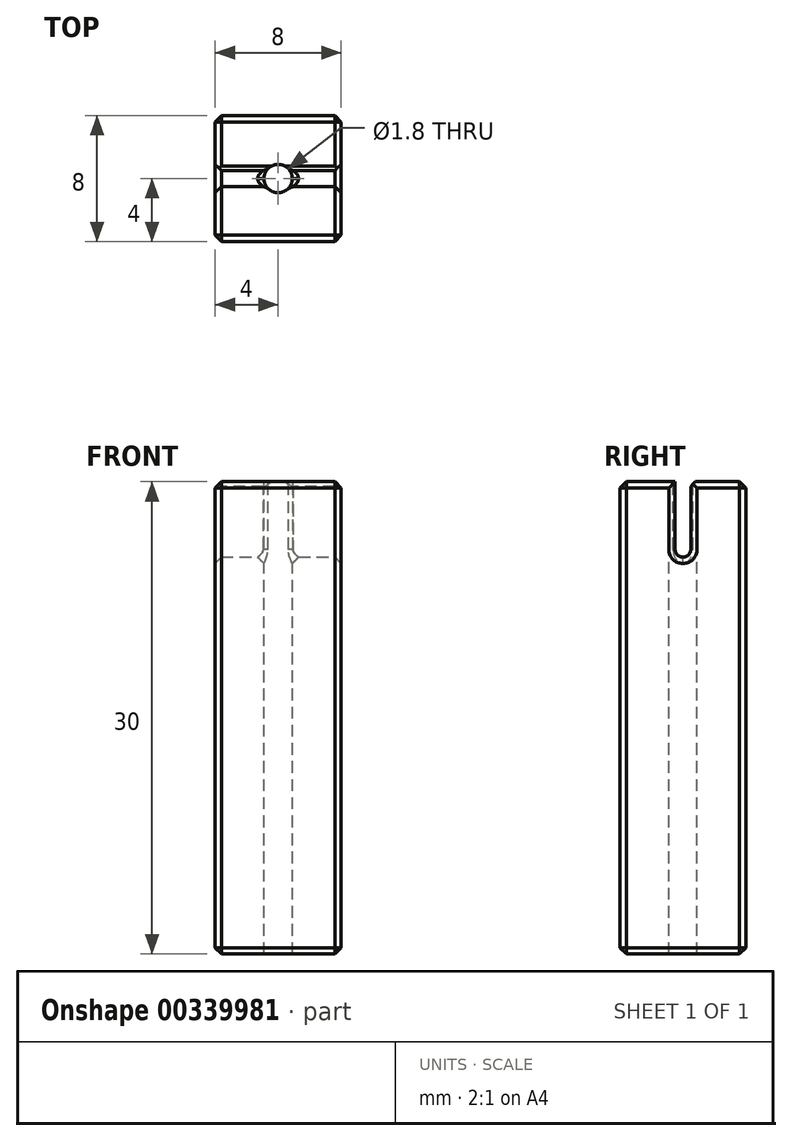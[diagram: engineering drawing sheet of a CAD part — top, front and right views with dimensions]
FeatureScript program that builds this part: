
annotation { "Feature Type Name" : "Feature", "Feature Type Description" : "" }
export const myFeature = defineFeature(function(context is Context, id is Id, definition is map)
    precondition{}
    {
        {
            var Q0;
            Q0=qCreatedBy(makeId("Top.planeOp"),FACE);
            var sketch = newSketch(context, id + "F0", { "sketchPlane" : qUnion([Q0])});
            skLineSegment(sketch, "E0.bottom", {"start": v(4, -4) * mm, "end": v(-4, -4) * mm});
            skLineSegment(sketch, "E0.top", {"start": v(4, 4) * mm, "end": v(-4, 4) * mm});
            skLineSegment(sketch, "E0.left", {"start": v(4, -4) * mm, "end": v(4, 4) * mm});
            skLineSegment(sketch, "E0.right", {"start": v(-4, -4) * mm, "end": v(-4, 4) * mm});
            skPoint(sketch, "E0.middle", {"position": v(0, 0) * mm});
            skSolve(sketch);
        }
        {
            var Q0;
            Q0=qSketchRegion(id+"F0",true);
            extrude(context, id + "F1", {"entities" : qUnion([Q0]), "depth" : 15 * mm, "hasSecondDirection" : true, "secondDirectionOppositeDirection" : true, "secondDirectionDepth" : 15 * mm});
        }
        {
            var Q0;
            Q0=makeQuery(id+"F1.opExtrude","CAP_FACE",FACE,{"disambiguationData":[OSD([sQuery(id+"F0.wireOp",EDGE,"E0.bottom"),sQuery(id+"F0.wireOp",EDGE,"E0.top"),sQuery(id+"F0.wireOp",EDGE,"E0.left"),sQuery(id+"F0.wireOp",EDGE,"E0.right")])],"isStart":false});
            var sketch = newSketch(context, id + "F2", { "sketchPlane" : qUnion([Q0])});
            skCircle(sketch, "E1", {"center": v(0, 0) * mm, "radius": 0.9 * mm});
            skSolve(sketch);
        }
        {
            var Q0;
            Q0=qSketchRegion(id+"F2",true);
            extrude(context, id + "F3", {"entities" : qUnion([Q0]), "operationType" : NewBodyOperationType.REMOVE, "oppositeDirection" : true, "depth" : 36.9 * mm});
        }
        {
            var Q0;
            Q0=makeQuery(id+"F1.opExtrude","CAP_FACE",FACE,{"disambiguationData":[OSD([sQuery(id+"F0.wireOp",EDGE,"E0.bottom"),sQuery(id+"F0.wireOp",EDGE,"E0.top"),sQuery(id+"F0.wireOp",EDGE,"E0.left"),sQuery(id+"F0.wireOp",EDGE,"E0.right")])],"isStart":false});
            var sketch = newSketch(context, id + "F4", { "sketchPlane" : qUnion([Q0])});
            skLineSegment(sketch, "E2.bottom", {"start": v(-5, -0.5) * mm, "end": v(5, -0.5) * mm});
            skLineSegment(sketch, "E2.top", {"start": v(-5, 0.5) * mm, "end": v(5, 0.5) * mm});
            skLineSegment(sketch, "E2.left", {"start": v(-5, -0.5) * mm, "end": v(-5, 0.5) * mm});
            skLineSegment(sketch, "E2.right", {"start": v(5, -0.5) * mm, "end": v(5, 0.5) * mm});
            skPoint(sketch, "E2.middle", {"position": v(0, 0) * mm});
            skLineSegment(sketch, "E3.bottom", {"start": v(-0.5, -5) * mm, "end": v(0.5, -5) * mm});
            skLineSegment(sketch, "E3.top", {"start": v(-0.5, 5) * mm, "end": v(0.5, 5) * mm});
            skLineSegment(sketch, "E3.left", {"start": v(-0.5, -5) * mm, "end": v(-0.5, 5) * mm});
            skLineSegment(sketch, "E3.right", {"start": v(0.5, -5) * mm, "end": v(0.5, 5) * mm});
            skSolve(sketch);
        }
        {
            var Q0;
            {var subQ0=sQuery(id+"F4.wireOp",EDGE,"E3.left");var subQ1=sQuery(id+"F4.wireOp",EDGE,"E2.bottom");var subQ2=makeQuery(id+"F4.imprint","INTERSECT",VERTEX,{"derivedFrom":[subQ1,subQ0]});Q0=makeQuery(id+"F4.imprint","IMPRINT",FACE,{"disambiguationData":[TD([[makeQuery(id+"F4.imprint","IMPRINT",EDGE,{"disambiguationData":[TD([[subQ2,-1.0]])],"derivedFrom":subQ1}),1.0]])]});}
            var Q1;
            {var subQ0=sQuery(id+"F4.wireOp",EDGE,"E2.left");Q1=makeQuery(id+"F4.imprint","IMPRINT",FACE,{"disambiguationData":[TD([[makeQuery(id+"F4.imprint","IMPRINT",EDGE,{"derivedFrom":subQ0}),-1.0]])]});}
            var Q2;
            {var subQ0=sQuery(id+"F4.wireOp",EDGE,"E2.right");Q2=makeQuery(id+"F4.imprint","IMPRINT",FACE,{"disambiguationData":[TD([[makeQuery(id+"F4.imprint","IMPRINT",EDGE,{"derivedFrom":subQ0}),1.0]])]});}
            var Q3;
            {var subQ0=sQuery(id+"F4.wireOp",EDGE,"E3.bottom");Q3=makeQuery(id+"F4.imprint","IMPRINT",FACE,{"disambiguationData":[TD([[makeQuery(id+"F4.imprint","IMPRINT",EDGE,{"derivedFrom":subQ0}),1.0]])]});}
            var Q4;
            {var subQ0=sQuery(id+"F4.wireOp",EDGE,"E3.top");Q4=makeQuery(id+"F4.imprint","IMPRINT",FACE,{"disambiguationData":[TD([[makeQuery(id+"F4.imprint","IMPRINT",EDGE,{"derivedFrom":subQ0}),-1.0]])]});}
            var Q5;
            {var subQ0=sQuery(id+"F4.wireOp",EDGE,"E3.left");var subQ1=sQuery(id+"F4.wireOp",EDGE,"E2.bottom");var subQ2=makeQuery(id+"F4.imprint","INTERSECT",VERTEX,{"derivedFrom":[subQ1,subQ0]});Q5=makeQuery(id+"F4.imprint","IMPRINT",FACE,{"disambiguationData":[TD([[makeQuery(id+"F4.imprint","IMPRINT",EDGE,{"disambiguationData":[TD([[subQ2,1.0]])],"derivedFrom":subQ1}),1.0]])]});}
            var Q6;
            {var subQ0=sQuery(id+"F4.wireOp",EDGE,"E3.left");var subQ1=sQuery(id+"F4.wireOp",EDGE,"E2.bottom");var subQ2=makeQuery(id+"F4.imprint","INTERSECT",VERTEX,{"derivedFrom":[subQ1,subQ0]});Q6=makeQuery(id+"F4.imprint","IMPRINT",FACE,{"disambiguationData":[TD([[makeQuery(id+"F4.imprint","IMPRINT",EDGE,{"disambiguationData":[TD([[subQ2,-1.0]])],"derivedFrom":subQ1}),-1.0]])]});}
            var Q7;
            {var subQ0=sQuery(id+"F4.wireOp",EDGE,"E3.right");var subQ1=sQuery(id+"F4.wireOp",EDGE,"E2.bottom");var subQ2=makeQuery(id+"F4.imprint","INTERSECT",VERTEX,{"derivedFrom":[subQ1,subQ0]});Q7=makeQuery(id+"F4.imprint","IMPRINT",FACE,{"disambiguationData":[TD([[makeQuery(id+"F4.imprint","IMPRINT",EDGE,{"disambiguationData":[TD([[subQ2,-1.0]])],"derivedFrom":subQ1}),1.0]])]});}
            var Q8;
            {var subQ0=sQuery(id+"F4.wireOp",EDGE,"E3.left");var subQ1=sQuery(id+"F4.wireOp",EDGE,"E2.top");var subQ2=makeQuery(id+"F4.imprint","INTERSECT",VERTEX,{"derivedFrom":[subQ1,subQ0]});Q8=makeQuery(id+"F4.imprint","IMPRINT",FACE,{"disambiguationData":[TD([[makeQuery(id+"F4.imprint","IMPRINT",EDGE,{"disambiguationData":[TD([[subQ2,-1.0]])],"derivedFrom":subQ1}),1.0]])]});}
            var Q9;
            {var subQ0=sQuery(id+"F4.wireOp",EDGE,"E2.bottom");var subQ1=makeQuery(id+"F1.opExtrude","CAP_EDGE",EDGE,{"disambiguationData":[OSD([sQuery(id+"F0.wireOp",EDGE,"E0.right")])],"isStart":false});var subQ2=makeQuery(id+"F4.imprint","INTERSECT",VERTEX,{"derivedFrom":[subQ1,subQ0]});Q9=makeQuery(id+"F4.imprint","IMPRINT",FACE,{"disambiguationData":[TD([[makeQuery(id+"F4.imprint","IMPRINT",EDGE,{"disambiguationData":[TD([[subQ2,-1.0]])],"derivedFrom":subQ0}),1.0]])]});}
            var Q10;
            {var subQ0=sQuery(id+"F4.wireOp",EDGE,"E2.bottom");var subQ1=makeQuery(id+"F1.opExtrude","CAP_EDGE",EDGE,{"disambiguationData":[OSD([sQuery(id+"F0.wireOp",EDGE,"E0.left")])],"isStart":false});var subQ2=makeQuery(id+"F4.imprint","INTERSECT",VERTEX,{"derivedFrom":[subQ1,subQ0]});Q10=makeQuery(id+"F4.imprint","IMPRINT",FACE,{"disambiguationData":[TD([[makeQuery(id+"F4.imprint","IMPRINT",EDGE,{"disambiguationData":[TD([[subQ2,1.0]])],"derivedFrom":subQ0}),1.0]])]});}
            extrude(context, id + "F5", {"entities" : qUnion([Q0, Q1, Q2, Q3, Q4, Q5, Q6, Q7, Q8, Q9, Q10]), "operationType" : NewBodyOperationType.REMOVE, "oppositeDirection" : true, "depth" : 4.8 * mm});
        }
        {
            var Q0;
            {var subQ0=sQuery(id+"F4.wireOp",EDGE,"E2.bottom");var subQ2=makeQuery(id+"F4.imprint","INTERSECT",VERTEX,{"derivedFrom":[makeQuery(id+"F1.opExtrude","CAP_EDGE",EDGE,{"disambiguationData":[OSD([sQuery(id+"F0.wireOp",EDGE,"E0.right")])],"isStart":false}),subQ0]});Q0=makeQuery(id+"F5.boolean.opBoolean","COPY",EDGE,{"derivedFrom":makeQuery(id+"F5.opExtrude","CAP_EDGE",EDGE,{"disambiguationData":[OSD([subQ0]),TDD([makeQuery(id+"F4.imprint","IMPRINT",EDGE,{"disambiguationData":[TD([[makeQuery(id+"F4.imprint","INTERSECT",VERTEX,{"derivedFrom":[subQ0,sQuery(id+"F4.wireOp",EDGE,"E2.left")]}),-1.0]])],"derivedFrom":subQ0}),makeQuery(id+"F4.imprint","IMPRINT",EDGE,{"disambiguationData":[TD([[subQ2,-1.0]])],"derivedFrom":subQ0}),makeQuery(id+"F4.imprint","IMPRINT",EDGE,{"disambiguationData":[TD([[makeQuery(id+"F4.imprint","INTERSECT",VERTEX,{"derivedFrom":[subQ0,sQuery(id+"F4.wireOp",EDGE,"E3.left")]}),1.0]])],"derivedFrom":subQ0})])],"isStart":false})});}
            var Q1;
            {var subQ0=sQuery(id+"F4.wireOp",EDGE,"E2.top");var subQ2=makeQuery(id+"F4.imprint","INTERSECT",VERTEX,{"derivedFrom":[makeQuery(id+"F1.opExtrude","CAP_EDGE",EDGE,{"disambiguationData":[OSD([sQuery(id+"F0.wireOp",EDGE,"E0.right")])],"isStart":false}),subQ0]});Q1=makeQuery(id+"F5.boolean.opBoolean","COPY",EDGE,{"derivedFrom":makeQuery(id+"F5.opExtrude","CAP_EDGE",EDGE,{"disambiguationData":[OSD([subQ0]),TDD([makeQuery(id+"F4.imprint","IMPRINT",EDGE,{"disambiguationData":[TD([[makeQuery(id+"F4.imprint","INTERSECT",VERTEX,{"derivedFrom":[subQ0,sQuery(id+"F4.wireOp",EDGE,"E2.left")]}),-1.0]])],"derivedFrom":subQ0}),makeQuery(id+"F4.imprint","IMPRINT",EDGE,{"disambiguationData":[TD([[subQ2,-1.0]])],"derivedFrom":subQ0}),makeQuery(id+"F4.imprint","IMPRINT",EDGE,{"disambiguationData":[TD([[makeQuery(id+"F4.imprint","INTERSECT",VERTEX,{"derivedFrom":[subQ0,sQuery(id+"F4.wireOp",EDGE,"E3.left")]}),1.0]])],"derivedFrom":subQ0})])],"isStart":false})});}
            var Q2;
            {var subQ0=sQuery(id+"F4.wireOp",EDGE,"E2.bottom");var subQ1=makeQuery(id+"F4.imprint","INTERSECT",VERTEX,{"derivedFrom":[makeQuery(id+"F1.opExtrude","CAP_EDGE",EDGE,{"disambiguationData":[OSD([sQuery(id+"F0.wireOp",EDGE,"E0.left")])],"isStart":false}),subQ0]});Q2=makeQuery(id+"F5.boolean.opBoolean","COPY",EDGE,{"derivedFrom":makeQuery(id+"F5.opExtrude","CAP_EDGE",EDGE,{"disambiguationData":[OSD([subQ0]),TDD([makeQuery(id+"F4.imprint","IMPRINT",EDGE,{"disambiguationData":[TD([[makeQuery(id+"F4.imprint","INTERSECT",VERTEX,{"derivedFrom":[subQ0,sQuery(id+"F4.wireOp",EDGE,"E3.right")]}),-1.0]])],"derivedFrom":subQ0}),makeQuery(id+"F4.imprint","IMPRINT",EDGE,{"disambiguationData":[TD([[subQ1,1.0]])],"derivedFrom":subQ0}),makeQuery(id+"F4.imprint","IMPRINT",EDGE,{"disambiguationData":[TD([[makeQuery(id+"F4.imprint","INTERSECT",VERTEX,{"derivedFrom":[subQ0,sQuery(id+"F4.wireOp",EDGE,"E2.right")]}),1.0]])],"derivedFrom":subQ0})])],"isStart":false})});}
            var Q3;
            {var subQ0=sQuery(id+"F4.wireOp",EDGE,"E2.top");var subQ1=makeQuery(id+"F4.imprint","INTERSECT",VERTEX,{"derivedFrom":[makeQuery(id+"F1.opExtrude","CAP_EDGE",EDGE,{"disambiguationData":[OSD([sQuery(id+"F0.wireOp",EDGE,"E0.left")])],"isStart":false}),subQ0]});Q3=makeQuery(id+"F5.boolean.opBoolean","COPY",EDGE,{"derivedFrom":makeQuery(id+"F5.opExtrude","CAP_EDGE",EDGE,{"disambiguationData":[OSD([subQ0]),TDD([makeQuery(id+"F4.imprint","IMPRINT",EDGE,{"disambiguationData":[TD([[makeQuery(id+"F4.imprint","INTERSECT",VERTEX,{"derivedFrom":[subQ0,sQuery(id+"F4.wireOp",EDGE,"E3.right")]}),-1.0]])],"derivedFrom":subQ0}),makeQuery(id+"F4.imprint","IMPRINT",EDGE,{"disambiguationData":[TD([[subQ1,1.0]])],"derivedFrom":subQ0}),makeQuery(id+"F4.imprint","IMPRINT",EDGE,{"disambiguationData":[TD([[makeQuery(id+"F4.imprint","INTERSECT",VERTEX,{"derivedFrom":[subQ0,sQuery(id+"F4.wireOp",EDGE,"E2.right")]}),1.0]])],"derivedFrom":subQ0})])],"isStart":false})});}
            var Q4;
            {var subQ0=sQuery(id+"F4.wireOp",EDGE,"E2.bottom");var subQ2=makeQuery(id+"F4.imprint","INTERSECT",VERTEX,{"derivedFrom":[makeQuery(id+"F1.opExtrude","CAP_EDGE",EDGE,{"disambiguationData":[OSD([sQuery(id+"F0.wireOp",EDGE,"E0.right")])],"isStart":false}),subQ0]});Q4=makeQuery(id+"FGitmNMdiUcegod_1.1.F5.boolean.opBoolean","COPY",EDGE,{"derivedFrom":makeQuery(id+"FGitmNMdiUcegod_1.1.F5.opExtrude","CAP_EDGE",EDGE,{"disambiguationData":[OSD([subQ0]),TDD([makeQuery(id+"F4.imprint","IMPRINT",EDGE,{"disambiguationData":[TD([[makeQuery(id+"F4.imprint","INTERSECT",VERTEX,{"derivedFrom":[subQ0,sQuery(id+"F4.wireOp",EDGE,"E2.left")]}),-1.0]])],"derivedFrom":subQ0}),makeQuery(id+"F4.imprint","IMPRINT",EDGE,{"disambiguationData":[TD([[subQ2,-1.0]])],"derivedFrom":subQ0}),makeQuery(id+"F4.imprint","IMPRINT",EDGE,{"disambiguationData":[TD([[makeQuery(id+"F4.imprint","INTERSECT",VERTEX,{"derivedFrom":[subQ0,sQuery(id+"F4.wireOp",EDGE,"E3.left")]}),1.0]])],"derivedFrom":subQ0})])],"isStart":false})});}
            var Q5;
            {var subQ0=sQuery(id+"F4.wireOp",EDGE,"E2.top");var subQ1=makeQuery(id+"F4.imprint","INTERSECT",VERTEX,{"derivedFrom":[makeQuery(id+"F1.opExtrude","CAP_EDGE",EDGE,{"disambiguationData":[OSD([sQuery(id+"F0.wireOp",EDGE,"E0.left")])],"isStart":false}),subQ0]});Q5=makeQuery(id+"FGitmNMdiUcegod_1.1.F5.boolean.opBoolean","COPY",EDGE,{"derivedFrom":makeQuery(id+"FGitmNMdiUcegod_1.1.F5.opExtrude","CAP_EDGE",EDGE,{"disambiguationData":[OSD([subQ0]),TDD([makeQuery(id+"F4.imprint","IMPRINT",EDGE,{"disambiguationData":[TD([[makeQuery(id+"F4.imprint","INTERSECT",VERTEX,{"derivedFrom":[subQ0,sQuery(id+"F4.wireOp",EDGE,"E3.right")]}),-1.0]])],"derivedFrom":subQ0}),makeQuery(id+"F4.imprint","IMPRINT",EDGE,{"disambiguationData":[TD([[subQ1,1.0]])],"derivedFrom":subQ0}),makeQuery(id+"F4.imprint","IMPRINT",EDGE,{"disambiguationData":[TD([[makeQuery(id+"F4.imprint","INTERSECT",VERTEX,{"derivedFrom":[subQ0,sQuery(id+"F4.wireOp",EDGE,"E2.right")]}),1.0]])],"derivedFrom":subQ0})])],"isStart":false})});}
            var Q6;
            {var subQ0=sQuery(id+"F4.wireOp",EDGE,"E2.bottom");var subQ1=makeQuery(id+"F4.imprint","INTERSECT",VERTEX,{"derivedFrom":[makeQuery(id+"F1.opExtrude","CAP_EDGE",EDGE,{"disambiguationData":[OSD([sQuery(id+"F0.wireOp",EDGE,"E0.left")])],"isStart":false}),subQ0]});Q6=makeQuery(id+"FGitmNMdiUcegod_1.1.F5.boolean.opBoolean","COPY",EDGE,{"derivedFrom":makeQuery(id+"FGitmNMdiUcegod_1.1.F5.opExtrude","CAP_EDGE",EDGE,{"disambiguationData":[OSD([subQ0]),TDD([makeQuery(id+"F4.imprint","IMPRINT",EDGE,{"disambiguationData":[TD([[makeQuery(id+"F4.imprint","INTERSECT",VERTEX,{"derivedFrom":[subQ0,sQuery(id+"F4.wireOp",EDGE,"E3.right")]}),-1.0]])],"derivedFrom":subQ0}),makeQuery(id+"F4.imprint","IMPRINT",EDGE,{"disambiguationData":[TD([[subQ1,1.0]])],"derivedFrom":subQ0}),makeQuery(id+"F4.imprint","IMPRINT",EDGE,{"disambiguationData":[TD([[makeQuery(id+"F4.imprint","INTERSECT",VERTEX,{"derivedFrom":[subQ0,sQuery(id+"F4.wireOp",EDGE,"E2.right")]}),1.0]])],"derivedFrom":subQ0})])],"isStart":false})});}
            var Q7;
            {var subQ0=sQuery(id+"F4.wireOp",EDGE,"E2.top");var subQ2=makeQuery(id+"F4.imprint","INTERSECT",VERTEX,{"derivedFrom":[makeQuery(id+"F1.opExtrude","CAP_EDGE",EDGE,{"disambiguationData":[OSD([sQuery(id+"F0.wireOp",EDGE,"E0.right")])],"isStart":false}),subQ0]});Q7=makeQuery(id+"FGitmNMdiUcegod_1.1.F5.boolean.opBoolean","COPY",EDGE,{"derivedFrom":makeQuery(id+"FGitmNMdiUcegod_1.1.F5.opExtrude","CAP_EDGE",EDGE,{"disambiguationData":[OSD([subQ0]),TDD([makeQuery(id+"F4.imprint","IMPRINT",EDGE,{"disambiguationData":[TD([[makeQuery(id+"F4.imprint","INTERSECT",VERTEX,{"derivedFrom":[subQ0,sQuery(id+"F4.wireOp",EDGE,"E2.left")]}),-1.0]])],"derivedFrom":subQ0}),makeQuery(id+"F4.imprint","IMPRINT",EDGE,{"disambiguationData":[TD([[subQ2,-1.0]])],"derivedFrom":subQ0}),makeQuery(id+"F4.imprint","IMPRINT",EDGE,{"disambiguationData":[TD([[makeQuery(id+"F4.imprint","INTERSECT",VERTEX,{"derivedFrom":[subQ0,sQuery(id+"F4.wireOp",EDGE,"E3.left")]}),1.0]])],"derivedFrom":subQ0})])],"isStart":false})});}
            fillet(context, id + "F6", {"entities" : qUnion([Q0, Q1, Q2, Q3, Q4, Q5, Q6, Q7]), "radius" : 0.5 * mm, "tangentPropagation" : true, "allowEdgeOverflow" : false});
        }
        {
            var Q0;
            {var subQ0=sQuery(id+"F0.wireOp",EDGE,"E0.bottom");var subQ1=sQuery(id+"F0.wireOp",EDGE,"E0.right");Q0=makeQuery(id+"FGitmNMdiUcegod_1.1.F5.boolean.opBoolean","SPLIT",EDGE,{"disambiguationData":[TD([makeQuery(id+"F1.opExtrude","SWEPT_FACE",FACE,{"disambiguationData":[OSD([subQ0])]})])],"derivedFrom":makeQuery(id+"F1.opExtrude","CAP_EDGE",EDGE,{"disambiguationData":[OSD([subQ1])],"isStart":true})});}
            var Q1;
            {var subQ0=sQuery(id+"F0.wireOp",EDGE,"E0.bottom");var subQ1=sQuery(id+"F0.wireOp",EDGE,"E0.left");Q1=makeQuery(id+"FGitmNMdiUcegod_1.1.F5.boolean.opBoolean","SPLIT",EDGE,{"disambiguationData":[TD([makeQuery(id+"F1.opExtrude","SWEPT_FACE",FACE,{"disambiguationData":[OSD([subQ0])]})])],"derivedFrom":makeQuery(id+"F1.opExtrude","CAP_EDGE",EDGE,{"disambiguationData":[OSD([subQ1])],"isStart":true})});}
            var Q2;
            {var subQ0=sQuery(id+"F0.wireOp",EDGE,"E0.left");var subQ1=sQuery(id+"F0.wireOp",EDGE,"E0.top");Q2=makeQuery(id+"FGitmNMdiUcegod_1.1.F5.boolean.opBoolean","SPLIT",EDGE,{"disambiguationData":[TD([makeQuery(id+"F1.opExtrude","SWEPT_FACE",FACE,{"disambiguationData":[OSD([subQ1])]})])],"derivedFrom":makeQuery(id+"F1.opExtrude","CAP_EDGE",EDGE,{"disambiguationData":[OSD([subQ0])],"isStart":true})});}
            var Q3;
            {var subQ0=sQuery(id+"F0.wireOp",EDGE,"E0.right");var subQ1=sQuery(id+"F0.wireOp",EDGE,"E0.top");Q3=makeQuery(id+"FGitmNMdiUcegod_1.1.F5.boolean.opBoolean","SPLIT",EDGE,{"disambiguationData":[TD([makeQuery(id+"F1.opExtrude","SWEPT_FACE",FACE,{"disambiguationData":[OSD([subQ1])]})])],"derivedFrom":makeQuery(id+"F1.opExtrude","CAP_EDGE",EDGE,{"disambiguationData":[OSD([subQ0])],"isStart":true})});}
            var Q4;
            Q4=makeQuery(id+"F1.opExtrude","CAP_EDGE",EDGE,{"disambiguationData":[OSD([sQuery(id+"F0.wireOp",EDGE,"E0.top")])],"isStart":true});
            var Q5;
            Q5=makeQuery(id+"F1.opExtrude","CAP_EDGE",EDGE,{"disambiguationData":[OSD([sQuery(id+"F0.wireOp",EDGE,"E0.bottom")])],"isStart":true});
            var Q6;
            {var subQ0=sQuery(id+"F0.wireOp",EDGE,"E0.bottom");var subQ1=sQuery(id+"F0.wireOp",EDGE,"E0.right");var subQ4=makeQuery(id+"F1.opExtrude","CAP_EDGE",EDGE,{"disambiguationData":[OSD([subQ1])],"isStart":false});Q6=makeQuery(id+"F5.boolean.opBoolean","SPLIT",EDGE,{"disambiguationData":[TD([makeQuery(id+"F1.opExtrude","SWEPT_FACE",FACE,{"disambiguationData":[OSD([subQ0])]})])],"derivedFrom":subQ4});}
            var Q7;
            {var subQ0=sQuery(id+"F0.wireOp",EDGE,"E0.bottom");var subQ2=sQuery(id+"F0.wireOp",EDGE,"E0.left");var subQ3=makeQuery(id+"F1.opExtrude","CAP_EDGE",EDGE,{"disambiguationData":[OSD([subQ2])],"isStart":false});Q7=makeQuery(id+"F5.boolean.opBoolean","SPLIT",EDGE,{"disambiguationData":[TD([makeQuery(id+"F1.opExtrude","SWEPT_FACE",FACE,{"disambiguationData":[OSD([subQ0])]})])],"derivedFrom":subQ3});}
            var Q8;
            Q8=makeQuery(id+"F1.opExtrude","CAP_EDGE",EDGE,{"disambiguationData":[OSD([sQuery(id+"F0.wireOp",EDGE,"E0.bottom")])],"isStart":false});
            var Q9;
            {var subQ0=sQuery(id+"F0.wireOp",EDGE,"E0.right");var subQ1=sQuery(id+"F0.wireOp",EDGE,"E0.top");var subQ4=makeQuery(id+"F1.opExtrude","CAP_EDGE",EDGE,{"disambiguationData":[OSD([subQ0])],"isStart":false});Q9=makeQuery(id+"F5.boolean.opBoolean","SPLIT",EDGE,{"disambiguationData":[TD([makeQuery(id+"F1.opExtrude","SWEPT_FACE",FACE,{"disambiguationData":[OSD([subQ1])]})])],"derivedFrom":subQ4});}
            var Q10;
            {var subQ0=sQuery(id+"F0.wireOp",EDGE,"E0.left");var subQ1=sQuery(id+"F0.wireOp",EDGE,"E0.top");var subQ3=makeQuery(id+"F1.opExtrude","CAP_EDGE",EDGE,{"disambiguationData":[OSD([subQ0])],"isStart":false});Q10=makeQuery(id+"F5.boolean.opBoolean","SPLIT",EDGE,{"disambiguationData":[TD([makeQuery(id+"F1.opExtrude","SWEPT_FACE",FACE,{"disambiguationData":[OSD([subQ1])]})])],"derivedFrom":subQ3});}
            var Q11;
            Q11=makeQuery(id+"F1.opExtrude","CAP_EDGE",EDGE,{"disambiguationData":[OSD([sQuery(id+"F0.wireOp",EDGE,"E0.top")])],"isStart":false});
            var Q12;
            Q12=makeQuery(id+"F1.opExtrude","SWEPT_EDGE",EDGE,{"disambiguationData":[OSD([sQuery(id+"F0.wireOp",EDGE,"E0.top"),sQuery(id+"F0.wireOp",EDGE,"E0.right")])]});
            var Q13;
            Q13=makeQuery(id+"F1.opExtrude","SWEPT_EDGE",EDGE,{"disambiguationData":[OSD([sQuery(id+"F0.wireOp",EDGE,"E0.bottom"),sQuery(id+"F0.wireOp",EDGE,"E0.right")])]});
            var Q14;
            Q14=makeQuery(id+"F1.opExtrude","SWEPT_EDGE",EDGE,{"disambiguationData":[OSD([sQuery(id+"F0.wireOp",EDGE,"E0.top"),sQuery(id+"F0.wireOp",EDGE,"E0.left")])]});
            var Q15;
            Q15=makeQuery(id+"F1.opExtrude","SWEPT_EDGE",EDGE,{"disambiguationData":[OSD([sQuery(id+"F0.wireOp",EDGE,"E0.bottom"),sQuery(id+"F0.wireOp",EDGE,"E0.left")])]});
            var Q16;
            {var subQ0=sQuery(id+"F4.wireOp",EDGE,"E2.top");var subQ1=sQuery(id+"F0.wireOp",EDGE,"E0.left");var subQ2=makeQuery(id+"F4.imprint","INTERSECT",VERTEX,{"derivedFrom":[makeQuery(id+"F1.opExtrude","CAP_EDGE",EDGE,{"disambiguationData":[OSD([subQ1])],"isStart":false}),subQ0]});Q16=makeQuery(id+"F5.boolean.opBoolean","INTERSECT",EDGE,{"derivedFrom":[makeQuery(id+"F1.opExtrude","SWEPT_FACE",FACE,{"disambiguationData":[OSD([subQ1])]}),makeQuery(id+"F5.opExtrude","SWEPT_FACE",FACE,{"disambiguationData":[OSD([subQ0]),TDD([makeQuery(id+"F4.imprint","IMPRINT",EDGE,{"disambiguationData":[TD([[makeQuery(id+"F4.imprint","INTERSECT",VERTEX,{"derivedFrom":[subQ0,sQuery(id+"F4.wireOp",EDGE,"E3.right")]}),-1.0]])],"derivedFrom":subQ0}),makeQuery(id+"F4.imprint","IMPRINT",EDGE,{"disambiguationData":[TD([[subQ2,1.0]])],"derivedFrom":subQ0}),makeQuery(id+"F4.imprint","IMPRINT",EDGE,{"disambiguationData":[TD([[makeQuery(id+"F4.imprint","INTERSECT",VERTEX,{"derivedFrom":[subQ0,sQuery(id+"F4.wireOp",EDGE,"E2.right")]}),1.0]])],"derivedFrom":subQ0})])]})]});}
            var Q17;
            {var subQ0=sQuery(id+"F4.wireOp",EDGE,"E2.top");var subQ2=sQuery(id+"F0.wireOp",EDGE,"E0.right");var subQ3=makeQuery(id+"F4.imprint","INTERSECT",VERTEX,{"derivedFrom":[makeQuery(id+"F1.opExtrude","CAP_EDGE",EDGE,{"disambiguationData":[OSD([subQ2])],"isStart":false}),subQ0]});Q17=makeQuery(id+"F5.boolean.opBoolean","INTERSECT",EDGE,{"derivedFrom":[makeQuery(id+"F1.opExtrude","SWEPT_FACE",FACE,{"disambiguationData":[OSD([subQ2])]}),makeQuery(id+"F5.opExtrude","SWEPT_FACE",FACE,{"disambiguationData":[OSD([subQ0]),TDD([makeQuery(id+"F4.imprint","IMPRINT",EDGE,{"disambiguationData":[TD([[makeQuery(id+"F4.imprint","INTERSECT",VERTEX,{"derivedFrom":[subQ0,sQuery(id+"F4.wireOp",EDGE,"E2.left")]}),-1.0]])],"derivedFrom":subQ0}),makeQuery(id+"F4.imprint","IMPRINT",EDGE,{"disambiguationData":[TD([[subQ3,-1.0]])],"derivedFrom":subQ0}),makeQuery(id+"F4.imprint","IMPRINT",EDGE,{"disambiguationData":[TD([[makeQuery(id+"F4.imprint","INTERSECT",VERTEX,{"derivedFrom":[subQ0,sQuery(id+"F4.wireOp",EDGE,"E3.left")]}),1.0]])],"derivedFrom":subQ0})])]})]});}
            var Q18;
            {var subQ0=sQuery(id+"F4.wireOp",EDGE,"E2.top");var subQ2=sQuery(id+"F0.wireOp",EDGE,"E0.right");var subQ3=makeQuery(id+"F4.imprint","INTERSECT",VERTEX,{"derivedFrom":[makeQuery(id+"F1.opExtrude","CAP_EDGE",EDGE,{"disambiguationData":[OSD([subQ2])],"isStart":false}),subQ0]});Q18=makeQuery(id+"FGitmNMdiUcegod_1.1.F5.boolean.opBoolean","INTERSECT",EDGE,{"derivedFrom":[makeQuery(id+"F1.opExtrude","SWEPT_FACE",FACE,{"disambiguationData":[OSD([subQ2])]}),makeQuery(id+"FGitmNMdiUcegod_1.1.F5.opExtrude","SWEPT_FACE",FACE,{"disambiguationData":[OSD([subQ0]),TDD([makeQuery(id+"F4.imprint","IMPRINT",EDGE,{"disambiguationData":[TD([[makeQuery(id+"F4.imprint","INTERSECT",VERTEX,{"derivedFrom":[subQ0,sQuery(id+"F4.wireOp",EDGE,"E2.left")]}),-1.0]])],"derivedFrom":subQ0}),makeQuery(id+"F4.imprint","IMPRINT",EDGE,{"disambiguationData":[TD([[subQ3,-1.0]])],"derivedFrom":subQ0}),makeQuery(id+"F4.imprint","IMPRINT",EDGE,{"disambiguationData":[TD([[makeQuery(id+"F4.imprint","INTERSECT",VERTEX,{"derivedFrom":[subQ0,sQuery(id+"F4.wireOp",EDGE,"E3.left")]}),1.0]])],"derivedFrom":subQ0})])]})]});}
            var Q19;
            {var subQ0=sQuery(id+"F4.wireOp",EDGE,"E2.top");var subQ1=sQuery(id+"F0.wireOp",EDGE,"E0.left");var subQ2=makeQuery(id+"F4.imprint","INTERSECT",VERTEX,{"derivedFrom":[makeQuery(id+"F1.opExtrude","CAP_EDGE",EDGE,{"disambiguationData":[OSD([subQ1])],"isStart":false}),subQ0]});Q19=makeQuery(id+"FGitmNMdiUcegod_1.1.F5.boolean.opBoolean","INTERSECT",EDGE,{"derivedFrom":[makeQuery(id+"F1.opExtrude","SWEPT_FACE",FACE,{"disambiguationData":[OSD([subQ1])]}),makeQuery(id+"FGitmNMdiUcegod_1.1.F5.opExtrude","SWEPT_FACE",FACE,{"disambiguationData":[OSD([subQ0]),TDD([makeQuery(id+"F4.imprint","IMPRINT",EDGE,{"disambiguationData":[TD([[makeQuery(id+"F4.imprint","INTERSECT",VERTEX,{"derivedFrom":[subQ0,sQuery(id+"F4.wireOp",EDGE,"E3.right")]}),-1.0]])],"derivedFrom":subQ0}),makeQuery(id+"F4.imprint","IMPRINT",EDGE,{"disambiguationData":[TD([[subQ2,1.0]])],"derivedFrom":subQ0}),makeQuery(id+"F4.imprint","IMPRINT",EDGE,{"disambiguationData":[TD([[makeQuery(id+"F4.imprint","INTERSECT",VERTEX,{"derivedFrom":[subQ0,sQuery(id+"F4.wireOp",EDGE,"E2.right")]}),1.0]])],"derivedFrom":subQ0})])]})]});}
            chamfer(context, id + "F7", {"entities" : qUnion([Q0, Q1, Q2, Q3, Q4, Q5, Q6, Q7, Q8, Q9, Q10, Q11, Q12, Q13, Q14, Q15, Q16, Q17, Q18, Q19]), "width" : 0.4 * mm, "tangentPropagation" : true});
        }
        {
            var Q0;
            {var subQ0=sQuery(id+"F4.wireOp",EDGE,"E2.top");var subQ2=makeQuery(id+"F4.imprint","INTERSECT",VERTEX,{"derivedFrom":[makeQuery(id+"F1.opExtrude","CAP_EDGE",EDGE,{"disambiguationData":[OSD([sQuery(id+"F0.wireOp",EDGE,"E0.right")])],"isStart":false}),subQ0]});Q0=makeQuery(id+"F5.boolean.opBoolean","COPY",EDGE,{"derivedFrom":makeQuery(id+"F5.opExtrude","CAP_EDGE",EDGE,{"disambiguationData":[OSD([subQ0]),TDD([makeQuery(id+"F4.imprint","IMPRINT",EDGE,{"disambiguationData":[TD([[makeQuery(id+"F4.imprint","INTERSECT",VERTEX,{"derivedFrom":[subQ0,sQuery(id+"F4.wireOp",EDGE,"E2.left")]}),-1.0]])],"derivedFrom":subQ0}),makeQuery(id+"F4.imprint","IMPRINT",EDGE,{"disambiguationData":[TD([[subQ2,-1.0]])],"derivedFrom":subQ0}),makeQuery(id+"F4.imprint","IMPRINT",EDGE,{"disambiguationData":[TD([[makeQuery(id+"F4.imprint","INTERSECT",VERTEX,{"derivedFrom":[subQ0,sQuery(id+"F4.wireOp",EDGE,"E3.left")]}),1.0]])],"derivedFrom":subQ0})])],"isStart":true})});}
            var Q1;
            {var subQ0=sQuery(id+"F4.wireOp",EDGE,"E2.top");var subQ1=makeQuery(id+"F4.imprint","INTERSECT",VERTEX,{"derivedFrom":[makeQuery(id+"F1.opExtrude","CAP_EDGE",EDGE,{"disambiguationData":[OSD([sQuery(id+"F0.wireOp",EDGE,"E0.left")])],"isStart":false}),subQ0]});Q1=makeQuery(id+"F5.boolean.opBoolean","COPY",EDGE,{"derivedFrom":makeQuery(id+"F5.opExtrude","CAP_EDGE",EDGE,{"disambiguationData":[OSD([subQ0]),TDD([makeQuery(id+"F4.imprint","IMPRINT",EDGE,{"disambiguationData":[TD([[makeQuery(id+"F4.imprint","INTERSECT",VERTEX,{"derivedFrom":[subQ0,sQuery(id+"F4.wireOp",EDGE,"E3.right")]}),-1.0]])],"derivedFrom":subQ0}),makeQuery(id+"F4.imprint","IMPRINT",EDGE,{"disambiguationData":[TD([[subQ1,1.0]])],"derivedFrom":subQ0}),makeQuery(id+"F4.imprint","IMPRINT",EDGE,{"disambiguationData":[TD([[makeQuery(id+"F4.imprint","INTERSECT",VERTEX,{"derivedFrom":[subQ0,sQuery(id+"F4.wireOp",EDGE,"E2.right")]}),1.0]])],"derivedFrom":subQ0})])],"isStart":true})});}
            var Q2;
            {var subQ0=sQuery(id+"F4.wireOp",EDGE,"E2.bottom");var subQ1=makeQuery(id+"F4.imprint","INTERSECT",VERTEX,{"derivedFrom":[makeQuery(id+"F1.opExtrude","CAP_EDGE",EDGE,{"disambiguationData":[OSD([sQuery(id+"F0.wireOp",EDGE,"E0.left")])],"isStart":false}),subQ0]});Q2=makeQuery(id+"F5.boolean.opBoolean","COPY",EDGE,{"derivedFrom":makeQuery(id+"F5.opExtrude","CAP_EDGE",EDGE,{"disambiguationData":[OSD([subQ0]),TDD([makeQuery(id+"F4.imprint","IMPRINT",EDGE,{"disambiguationData":[TD([[makeQuery(id+"F4.imprint","INTERSECT",VERTEX,{"derivedFrom":[subQ0,sQuery(id+"F4.wireOp",EDGE,"E3.right")]}),-1.0]])],"derivedFrom":subQ0}),makeQuery(id+"F4.imprint","IMPRINT",EDGE,{"disambiguationData":[TD([[subQ1,1.0]])],"derivedFrom":subQ0}),makeQuery(id+"F4.imprint","IMPRINT",EDGE,{"disambiguationData":[TD([[makeQuery(id+"F4.imprint","INTERSECT",VERTEX,{"derivedFrom":[subQ0,sQuery(id+"F4.wireOp",EDGE,"E2.right")]}),1.0]])],"derivedFrom":subQ0})])],"isStart":true})});}
            var Q3;
            {var subQ0=sQuery(id+"F4.wireOp",EDGE,"E2.bottom");var subQ2=makeQuery(id+"F4.imprint","INTERSECT",VERTEX,{"derivedFrom":[makeQuery(id+"F1.opExtrude","CAP_EDGE",EDGE,{"disambiguationData":[OSD([sQuery(id+"F0.wireOp",EDGE,"E0.right")])],"isStart":false}),subQ0]});Q3=makeQuery(id+"F5.boolean.opBoolean","COPY",EDGE,{"derivedFrom":makeQuery(id+"F5.opExtrude","CAP_EDGE",EDGE,{"disambiguationData":[OSD([subQ0]),TDD([makeQuery(id+"F4.imprint","IMPRINT",EDGE,{"disambiguationData":[TD([[makeQuery(id+"F4.imprint","INTERSECT",VERTEX,{"derivedFrom":[subQ0,sQuery(id+"F4.wireOp",EDGE,"E2.left")]}),-1.0]])],"derivedFrom":subQ0}),makeQuery(id+"F4.imprint","IMPRINT",EDGE,{"disambiguationData":[TD([[subQ2,-1.0]])],"derivedFrom":subQ0}),makeQuery(id+"F4.imprint","IMPRINT",EDGE,{"disambiguationData":[TD([[makeQuery(id+"F4.imprint","INTERSECT",VERTEX,{"derivedFrom":[subQ0,sQuery(id+"F4.wireOp",EDGE,"E3.left")]}),1.0]])],"derivedFrom":subQ0})])],"isStart":true})});}
            var Q4;
            {var subQ0=sQuery(id+"F4.wireOp",EDGE,"E2.top");var subQ1=makeQuery(id+"F4.imprint","INTERSECT",VERTEX,{"derivedFrom":[makeQuery(id+"F1.opExtrude","CAP_EDGE",EDGE,{"disambiguationData":[OSD([sQuery(id+"F0.wireOp",EDGE,"E0.left")])],"isStart":false}),subQ0]});Q4=makeQuery(id+"FGitmNMdiUcegod_1.1.F5.boolean.opBoolean","COPY",EDGE,{"derivedFrom":makeQuery(id+"FGitmNMdiUcegod_1.1.F5.opExtrude","CAP_EDGE",EDGE,{"disambiguationData":[OSD([subQ0]),TDD([makeQuery(id+"F4.imprint","IMPRINT",EDGE,{"disambiguationData":[TD([[makeQuery(id+"F4.imprint","INTERSECT",VERTEX,{"derivedFrom":[subQ0,sQuery(id+"F4.wireOp",EDGE,"E3.right")]}),-1.0]])],"derivedFrom":subQ0}),makeQuery(id+"F4.imprint","IMPRINT",EDGE,{"disambiguationData":[TD([[subQ1,1.0]])],"derivedFrom":subQ0}),makeQuery(id+"F4.imprint","IMPRINT",EDGE,{"disambiguationData":[TD([[makeQuery(id+"F4.imprint","INTERSECT",VERTEX,{"derivedFrom":[subQ0,sQuery(id+"F4.wireOp",EDGE,"E2.right")]}),1.0]])],"derivedFrom":subQ0})])],"isStart":true})});}
            var Q5;
            {var subQ0=sQuery(id+"F4.wireOp",EDGE,"E2.top");var subQ2=makeQuery(id+"F4.imprint","INTERSECT",VERTEX,{"derivedFrom":[makeQuery(id+"F1.opExtrude","CAP_EDGE",EDGE,{"disambiguationData":[OSD([sQuery(id+"F0.wireOp",EDGE,"E0.right")])],"isStart":false}),subQ0]});Q5=makeQuery(id+"FGitmNMdiUcegod_1.1.F5.boolean.opBoolean","COPY",EDGE,{"derivedFrom":makeQuery(id+"FGitmNMdiUcegod_1.1.F5.opExtrude","CAP_EDGE",EDGE,{"disambiguationData":[OSD([subQ0]),TDD([makeQuery(id+"F4.imprint","IMPRINT",EDGE,{"disambiguationData":[TD([[makeQuery(id+"F4.imprint","INTERSECT",VERTEX,{"derivedFrom":[subQ0,sQuery(id+"F4.wireOp",EDGE,"E2.left")]}),-1.0]])],"derivedFrom":subQ0}),makeQuery(id+"F4.imprint","IMPRINT",EDGE,{"disambiguationData":[TD([[subQ2,-1.0]])],"derivedFrom":subQ0}),makeQuery(id+"F4.imprint","IMPRINT",EDGE,{"disambiguationData":[TD([[makeQuery(id+"F4.imprint","INTERSECT",VERTEX,{"derivedFrom":[subQ0,sQuery(id+"F4.wireOp",EDGE,"E3.left")]}),1.0]])],"derivedFrom":subQ0})])],"isStart":true})});}
            var Q6;
            {var subQ0=sQuery(id+"F4.wireOp",EDGE,"E2.bottom");var subQ2=makeQuery(id+"F4.imprint","INTERSECT",VERTEX,{"derivedFrom":[makeQuery(id+"F1.opExtrude","CAP_EDGE",EDGE,{"disambiguationData":[OSD([sQuery(id+"F0.wireOp",EDGE,"E0.right")])],"isStart":false}),subQ0]});Q6=makeQuery(id+"FGitmNMdiUcegod_1.1.F5.boolean.opBoolean","COPY",EDGE,{"derivedFrom":makeQuery(id+"FGitmNMdiUcegod_1.1.F5.opExtrude","CAP_EDGE",EDGE,{"disambiguationData":[OSD([subQ0]),TDD([makeQuery(id+"F4.imprint","IMPRINT",EDGE,{"disambiguationData":[TD([[makeQuery(id+"F4.imprint","INTERSECT",VERTEX,{"derivedFrom":[subQ0,sQuery(id+"F4.wireOp",EDGE,"E2.left")]}),-1.0]])],"derivedFrom":subQ0}),makeQuery(id+"F4.imprint","IMPRINT",EDGE,{"disambiguationData":[TD([[subQ2,-1.0]])],"derivedFrom":subQ0}),makeQuery(id+"F4.imprint","IMPRINT",EDGE,{"disambiguationData":[TD([[makeQuery(id+"F4.imprint","INTERSECT",VERTEX,{"derivedFrom":[subQ0,sQuery(id+"F4.wireOp",EDGE,"E3.left")]}),1.0]])],"derivedFrom":subQ0})])],"isStart":true})});}
            var Q7;
            {var subQ0=sQuery(id+"F4.wireOp",EDGE,"E2.bottom");var subQ1=makeQuery(id+"F4.imprint","INTERSECT",VERTEX,{"derivedFrom":[makeQuery(id+"F1.opExtrude","CAP_EDGE",EDGE,{"disambiguationData":[OSD([sQuery(id+"F0.wireOp",EDGE,"E0.left")])],"isStart":false}),subQ0]});Q7=makeQuery(id+"FGitmNMdiUcegod_1.1.F5.boolean.opBoolean","COPY",EDGE,{"derivedFrom":makeQuery(id+"FGitmNMdiUcegod_1.1.F5.opExtrude","CAP_EDGE",EDGE,{"disambiguationData":[OSD([subQ0]),TDD([makeQuery(id+"F4.imprint","IMPRINT",EDGE,{"disambiguationData":[TD([[makeQuery(id+"F4.imprint","INTERSECT",VERTEX,{"derivedFrom":[subQ0,sQuery(id+"F4.wireOp",EDGE,"E3.right")]}),-1.0]])],"derivedFrom":subQ0}),makeQuery(id+"F4.imprint","IMPRINT",EDGE,{"disambiguationData":[TD([[subQ1,1.0]])],"derivedFrom":subQ0}),makeQuery(id+"F4.imprint","IMPRINT",EDGE,{"disambiguationData":[TD([[makeQuery(id+"F4.imprint","INTERSECT",VERTEX,{"derivedFrom":[subQ0,sQuery(id+"F4.wireOp",EDGE,"E2.right")]}),1.0]])],"derivedFrom":subQ0})])],"isStart":true})});}
            chamfer(context, id + "F8", {"entities" : qUnion([Q0, Q1, Q2, Q3, Q4, Q5, Q6, Q7]), "width" : 0.3 * mm, "tangentPropagation" : true});
        }
        {
            var Q0;
            {var subQ0=sQuery(id+"F2.wireOp",EDGE,"E1");var subQ1=sQuery(id+"F4.wireOp",EDGE,"E2.top");var subQ3=makeQuery(id+"F4.imprint","INTERSECT",VERTEX,{"derivedFrom":[makeQuery(id+"F1.opExtrude","CAP_EDGE",EDGE,{"disambiguationData":[OSD([sQuery(id+"F0.wireOp",EDGE,"E0.right")])],"isStart":false}),subQ1]});Q0=makeQuery(id+"F6.opFillet","BLEND_EDGE",EDGE,{"blendedFrom":[makeQuery(id+"FGitmNMdiUcegod_1.1.F5.boolean.opBoolean","COPY",EDGE,{"derivedFrom":makeQuery(id+"FGitmNMdiUcegod_1.1.F5.opExtrude","CAP_EDGE",EDGE,{"disambiguationData":[OSD([subQ1]),TDD([makeQuery(id+"F4.imprint","IMPRINT",EDGE,{"disambiguationData":[TD([[makeQuery(id+"F4.imprint","INTERSECT",VERTEX,{"derivedFrom":[subQ1,sQuery(id+"F4.wireOp",EDGE,"E2.left")]}),-1.0]])],"derivedFrom":subQ1}),makeQuery(id+"F4.imprint","IMPRINT",EDGE,{"disambiguationData":[TD([[subQ3,-1.0]])],"derivedFrom":subQ1}),makeQuery(id+"F4.imprint","IMPRINT",EDGE,{"disambiguationData":[TD([[makeQuery(id+"F4.imprint","INTERSECT",VERTEX,{"derivedFrom":[subQ1,sQuery(id+"F4.wireOp",EDGE,"E3.left")]}),1.0]])],"derivedFrom":subQ1})])],"isStart":false})}),makeQuery(id+"F3.boolean.opBoolean","COPY",FACE,{"derivedFrom":makeQuery(id+"F3.opExtrude","SWEPT_FACE",FACE,{"disambiguationData":[OSD([subQ0])]})})],"blendedInto":[makeQuery(id+"F3.boolean.opBoolean","COPY",FACE,{"derivedFrom":makeQuery(id+"F3.opExtrude","SWEPT_FACE",FACE,{"disambiguationData":[OSD([subQ0])]})})]});}
            var Q1;
            {var subQ0=sQuery(id+"F2.wireOp",EDGE,"E1");var subQ1=sQuery(id+"F4.wireOp",EDGE,"E2.top");var subQ2=makeQuery(id+"F4.imprint","INTERSECT",VERTEX,{"derivedFrom":[makeQuery(id+"F1.opExtrude","CAP_EDGE",EDGE,{"disambiguationData":[OSD([sQuery(id+"F0.wireOp",EDGE,"E0.left")])],"isStart":false}),subQ1]});Q1=makeQuery(id+"F6.opFillet","BLEND_EDGE",EDGE,{"blendedFrom":[makeQuery(id+"FGitmNMdiUcegod_1.1.F5.boolean.opBoolean","COPY",EDGE,{"derivedFrom":makeQuery(id+"FGitmNMdiUcegod_1.1.F5.opExtrude","CAP_EDGE",EDGE,{"disambiguationData":[OSD([subQ1]),TDD([makeQuery(id+"F4.imprint","IMPRINT",EDGE,{"disambiguationData":[TD([[makeQuery(id+"F4.imprint","INTERSECT",VERTEX,{"derivedFrom":[subQ1,sQuery(id+"F4.wireOp",EDGE,"E3.right")]}),-1.0]])],"derivedFrom":subQ1}),makeQuery(id+"F4.imprint","IMPRINT",EDGE,{"disambiguationData":[TD([[subQ2,1.0]])],"derivedFrom":subQ1}),makeQuery(id+"F4.imprint","IMPRINT",EDGE,{"disambiguationData":[TD([[makeQuery(id+"F4.imprint","INTERSECT",VERTEX,{"derivedFrom":[subQ1,sQuery(id+"F4.wireOp",EDGE,"E2.right")]}),1.0]])],"derivedFrom":subQ1})])],"isStart":false})}),makeQuery(id+"F3.boolean.opBoolean","COPY",FACE,{"derivedFrom":makeQuery(id+"F3.opExtrude","SWEPT_FACE",FACE,{"disambiguationData":[OSD([subQ0])]})})],"blendedInto":[makeQuery(id+"F3.boolean.opBoolean","COPY",FACE,{"derivedFrom":makeQuery(id+"F3.opExtrude","SWEPT_FACE",FACE,{"disambiguationData":[OSD([subQ0])]})})]});}
            var Q2;
            {var subQ0=sQuery(id+"F2.wireOp",EDGE,"E1");var subQ1=sQuery(id+"F4.wireOp",EDGE,"E2.bottom");var subQ2=makeQuery(id+"F4.imprint","INTERSECT",VERTEX,{"derivedFrom":[makeQuery(id+"F1.opExtrude","CAP_EDGE",EDGE,{"disambiguationData":[OSD([sQuery(id+"F0.wireOp",EDGE,"E0.left")])],"isStart":false}),subQ1]});Q2=makeQuery(id+"F6.opFillet","BLEND_EDGE",EDGE,{"blendedFrom":[makeQuery(id+"F5.boolean.opBoolean","COPY",EDGE,{"derivedFrom":makeQuery(id+"F5.opExtrude","CAP_EDGE",EDGE,{"disambiguationData":[OSD([subQ1]),TDD([makeQuery(id+"F4.imprint","IMPRINT",EDGE,{"disambiguationData":[TD([[makeQuery(id+"F4.imprint","INTERSECT",VERTEX,{"derivedFrom":[subQ1,sQuery(id+"F4.wireOp",EDGE,"E3.right")]}),-1.0]])],"derivedFrom":subQ1}),makeQuery(id+"F4.imprint","IMPRINT",EDGE,{"disambiguationData":[TD([[subQ2,1.0]])],"derivedFrom":subQ1}),makeQuery(id+"F4.imprint","IMPRINT",EDGE,{"disambiguationData":[TD([[makeQuery(id+"F4.imprint","INTERSECT",VERTEX,{"derivedFrom":[subQ1,sQuery(id+"F4.wireOp",EDGE,"E2.right")]}),1.0]])],"derivedFrom":subQ1})])],"isStart":false})}),makeQuery(id+"F3.boolean.opBoolean","COPY",FACE,{"derivedFrom":makeQuery(id+"F3.opExtrude","SWEPT_FACE",FACE,{"disambiguationData":[OSD([subQ0])]})})],"blendedInto":[makeQuery(id+"F3.boolean.opBoolean","COPY",FACE,{"derivedFrom":makeQuery(id+"F3.opExtrude","SWEPT_FACE",FACE,{"disambiguationData":[OSD([subQ0])]})})]});}
            var Q3;
            {var subQ0=sQuery(id+"F2.wireOp",EDGE,"E1");var subQ1=sQuery(id+"F4.wireOp",EDGE,"E2.bottom");var subQ3=makeQuery(id+"F4.imprint","INTERSECT",VERTEX,{"derivedFrom":[makeQuery(id+"F1.opExtrude","CAP_EDGE",EDGE,{"disambiguationData":[OSD([sQuery(id+"F0.wireOp",EDGE,"E0.right")])],"isStart":false}),subQ1]});Q3=makeQuery(id+"F6.opFillet","BLEND_EDGE",EDGE,{"blendedFrom":[makeQuery(id+"F5.boolean.opBoolean","COPY",EDGE,{"derivedFrom":makeQuery(id+"F5.opExtrude","CAP_EDGE",EDGE,{"disambiguationData":[OSD([subQ1]),TDD([makeQuery(id+"F4.imprint","IMPRINT",EDGE,{"disambiguationData":[TD([[makeQuery(id+"F4.imprint","INTERSECT",VERTEX,{"derivedFrom":[subQ1,sQuery(id+"F4.wireOp",EDGE,"E2.left")]}),-1.0]])],"derivedFrom":subQ1}),makeQuery(id+"F4.imprint","IMPRINT",EDGE,{"disambiguationData":[TD([[subQ3,-1.0]])],"derivedFrom":subQ1}),makeQuery(id+"F4.imprint","IMPRINT",EDGE,{"disambiguationData":[TD([[makeQuery(id+"F4.imprint","INTERSECT",VERTEX,{"derivedFrom":[subQ1,sQuery(id+"F4.wireOp",EDGE,"E3.left")]}),1.0]])],"derivedFrom":subQ1})])],"isStart":false})}),makeQuery(id+"F3.boolean.opBoolean","COPY",FACE,{"derivedFrom":makeQuery(id+"F3.opExtrude","SWEPT_FACE",FACE,{"disambiguationData":[OSD([subQ0])]})})],"blendedInto":[makeQuery(id+"F3.boolean.opBoolean","COPY",FACE,{"derivedFrom":makeQuery(id+"F3.opExtrude","SWEPT_FACE",FACE,{"disambiguationData":[OSD([subQ0])]})})]});}
            chamfer(context, id + "F9", {"entities" : qUnion([Q0, Q1, Q2, Q3]), "width" : 0.4 * mm, "tangentPropagation" : true});
        }
    });
